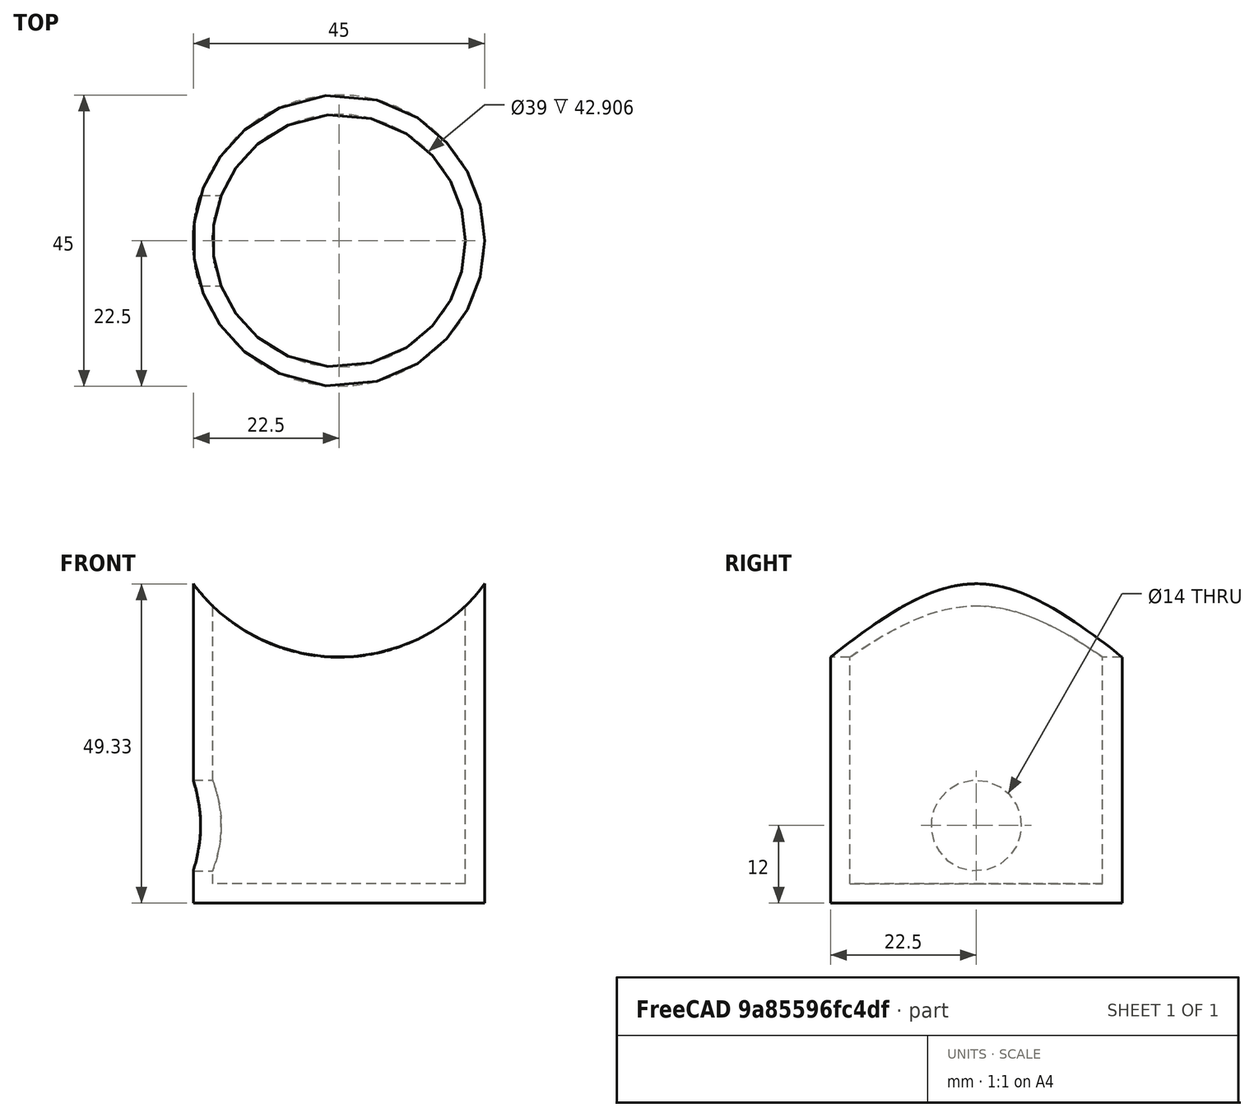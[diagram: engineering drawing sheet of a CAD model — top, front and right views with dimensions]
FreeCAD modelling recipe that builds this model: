
FCSTD DOCUMENT  (FreeCAD 0.18R4 (GitTag))
Label: impellerHousing
License: All rights reserved
LicenseURL: http://en.wikipedia.org/wiki/All_rights_reserved
objects: PartDesign::SubtractiveCylinder×3, PartDesign::AdditiveCylinder×2, PartDesign::Body×1
note: 11 computed .brp shape members not serialized (recipe doc carries the construction recipe); baked Part::Feature solids carry a one-line shape summary decoded from their .brp

FEATURE [PartDesign::AdditiveCylinder] Cylinder
  Angle = 360
  AttacherType = Attacher::AttachEngine3D
  Height = 50
  MapMode = 5
  Radius = 22.5
  Support = -> [XY_Plane]
FEATURE [PartDesign::SubtractiveCylinder] Cylinder001
  Angle = 360
  AttacherType = Attacher::AttachEngine3D
  AttachmentOffset = pos=(0,0,-5) rot=(0,0,1;0rad)
  BaseFeature = -> Cylinder
  Height = 60
  MapMode = 5
  Placement = pos=(0,0,-5) rot=(0,0,1;0rad)
  Radius = 19.5
  Support = -> [XY_Plane]
FEATURE [PartDesign::SubtractiveCylinder] Cylinder002
  Angle = 360
  AttacherType = Attacher::AttachEngine3D
  AttachmentOffset = pos=(0,26,66) rot=(1,0,0;1.5708rad)
  BaseFeature = -> Cylinder001
  Height = 54
  MapMode = 5
  Placement = pos=(0,26,66) rot=(1,0,0;1.5708rad)
  Radius = 28
  Support = -> [XY_Plane]
FEATURE [PartDesign::SubtractiveCylinder] Cylinder003
  Angle = 360
  AttacherType = Attacher::AttachEngine3D
  AttachmentOffset = pos=(0,12,-26) rot=(0,0,1;0rad)
  BaseFeature = -> Cylinder002
  Height = 10
  MapMode = 5
  Placement = pos=(-26,8.4e-15,12) rot=(0.57735,0.57735,0.57735;2.0944rad)
  Radius = 7
  Support = -> [YZ_Plane]
FEATURE [PartDesign::AdditiveCylinder] Cylinder004
  Angle = 360
  AttacherType = Attacher::AttachEngine3D
  BaseFeature = -> Cylinder003
  Height = 3
  Radius = 19.5
FEATURE [PartDesign::Body] Body
  Group = -> [Cylinder,Cylinder001,Cylinder002,Cylinder003,Cylinder004]
  Origin = -> Origin
  Tip = -> Cylinder004
